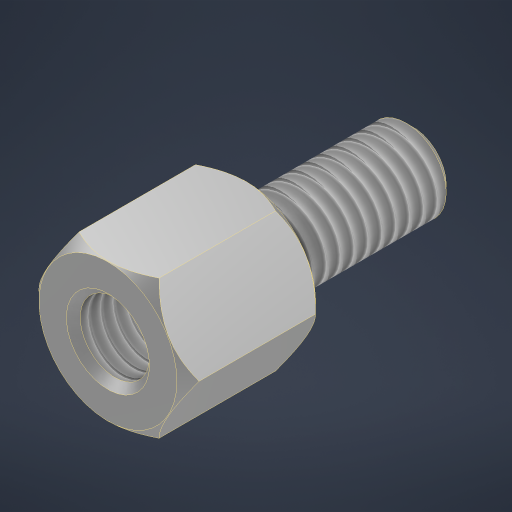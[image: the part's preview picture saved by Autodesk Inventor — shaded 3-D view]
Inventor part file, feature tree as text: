
AUTODESK INVENTOR PART (.ipt)
format: ipt  version: 2023 (Build 270158000, 158)  size: 251,904 bytes
history: native  units: in
note: dims shown in document units (in); Inventor stores cm internally (conversion verified against a paired STEP export)
features: thread x2, other x1
ambient origin geometry x8: Origin, YZ Plane, XZ Plane, XY Plane, X Axis, Y Axis, Z Axis, Center Point
bodies: Solid1 (feature_tree)
feature tree (3):
  thread  "Thread1"  [1 undecoded]
  thread  "Thread2"  [1 undecoded]
  other  "InnerChamfer"
note: 2 required parameter values undecoded (feature->parameter linkage not recoverable at this tier; creation-order binding heuristic only, values carry confidence <= 0.55)
